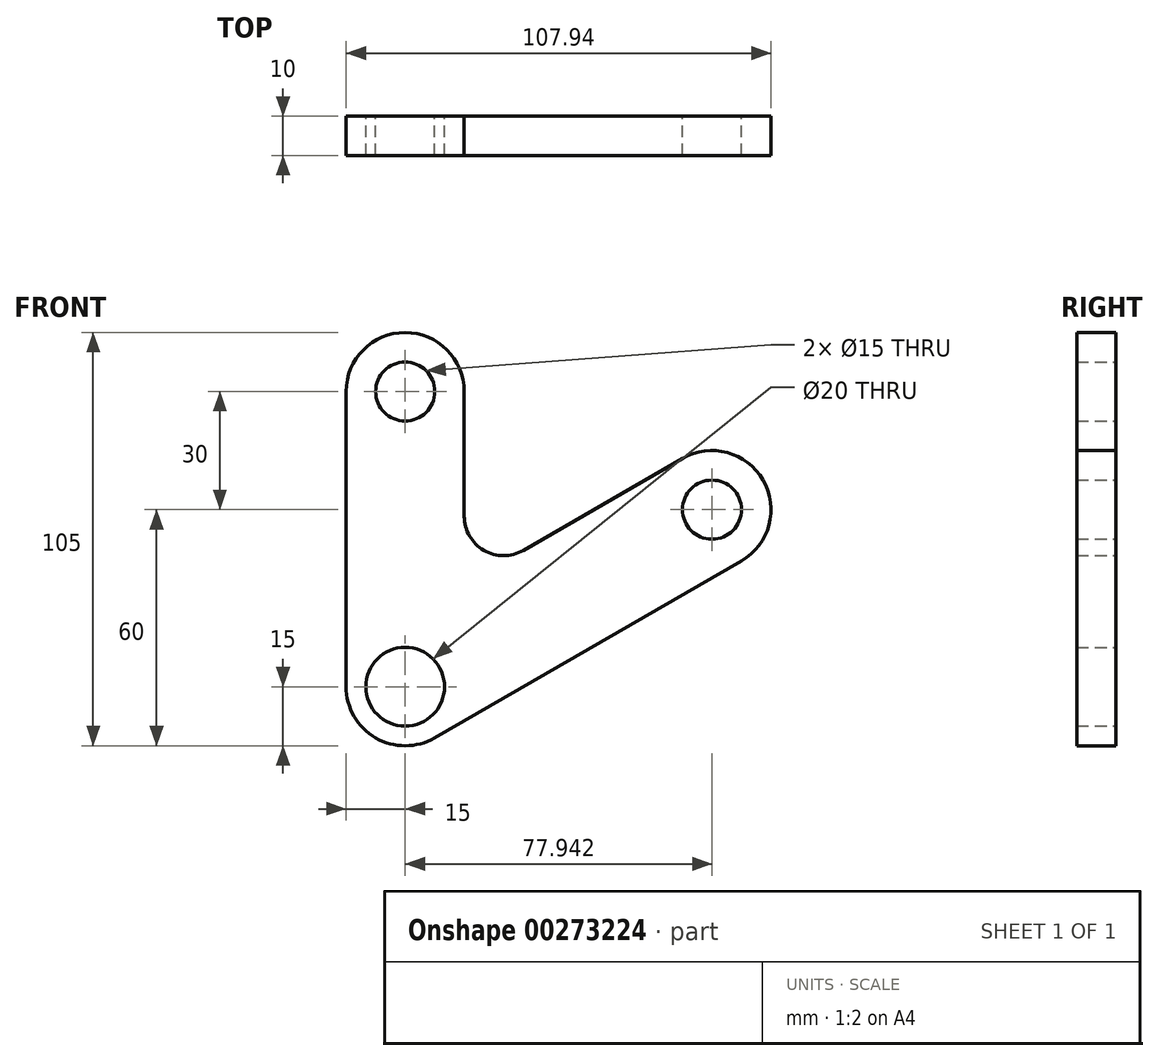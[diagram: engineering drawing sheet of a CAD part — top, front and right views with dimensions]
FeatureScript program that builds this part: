
annotation { "Feature Type Name" : "Feature", "Feature Type Description" : "" }
export const myFeature = defineFeature(function(context is Context, id is Id, definition is map)
    precondition{}
    {
        {
            var Q0;
            Q0=qCreatedBy(makeId("Front.planeOp"),FACE);
            var sketch = newSketch(context, id + "F0", { "sketchPlane" : qUnion([Q0])});
            skCircle(sketch, "E0", {"center": v(0, 0) * mm, "radius": 10 * mm});
            skCircle(sketch, "E1", {"center": v(0, 75) * mm, "radius": 7.5 * mm});
            skLineSegment(sketch, "E2", {"start": v(-15, 75) * mm, "end": v(-15, 0) * mm});
            skCircle(sketch, "E3", {"center": v(77.94, 45) * mm, "radius": 7.5 * mm});
            skArc(sketch, "E4", {"start": v(-15, 75) * mm, "mid": v(0, 90) * mm, "end": v(15, 75) * mm});
            skArc(sketch, "E5", {"start": v(85.44, 32) * mm, "mid": v(90.93, 52.5) * mm, "end": v(70.44, 58) * mm});
            skLineSegment(sketch, "E6", {"start": v(70.44, 58) * mm, "end": v(30, 34.64) * mm});
            skLineSegment(sketch, "E7", {"start": v(15, 75) * mm, "end": v(15, 43.3) * mm});
            skArc(sketch, "E8", {"start": v(15, 43.3) * mm, "mid": v(20, 34.64) * mm, "end": v(30, 34.64) * mm});
            skLineSegment(sketch, "E9", {"start": v(0, 75) * mm, "end": v(0, 0) * mm, "construction": true});
            skLineSegment(sketch, "E10", {"start": v(0, 0) * mm, "end": v(77.94, 45) * mm, "construction": true});
            skArc(sketch, "E11", {"start": v(-15, 0) * mm, "mid": v(-7.5, -13) * mm, "end": v(7.5, -13) * mm});
            skLineSegment(sketch, "E12", {"start": v(7.5, -13) * mm, "end": v(85.44, 32) * mm});
            skSolve(sketch);
        }
        {
            var Q0;
            Q0 = qSketchRegion(id + "F0", true);
            extrude(context, id + "F1", {"entities" : qUnion([Q0]), "depth" : 10 * mm});
        }
    });
